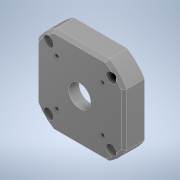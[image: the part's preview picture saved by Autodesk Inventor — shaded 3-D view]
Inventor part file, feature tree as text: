
AUTODESK INVENTOR PART (.ipt)
format: ipt  version: 2022 (Build 260153000, 153)  size: 180,224 bytes
history: mixed  units: in
note: dims shown in document units (in); Inventor stores cm internally (conversion verified against a paired STEP export)
features: extrude x2, sketch x2, chamfer x1, imported_body x1
ambient origin geometry x8: Origin, YZ Plane, XZ Plane, XY Plane, X Axis, Y Axis, Z Axis, Center Point
bodies: Solid1 (imported_parasolid)
feature tree (6):
  extrude  "Extrusion1"  Depth=0.3937in TaperAngle=0.0deg
  extrude  "Extrusion2"  Depth=0.3937in TaperAngle=0.0deg
  sketch  "Sketch1"  dims[d0=0.1102in d1=0.3937in d2=0.0in]
  sketch  "Sketch2"  dims[d3=0.5906in d4=0.3937in d5=0.0in]
  chamfer  "Chamfer2"  [1 undecoded]
  imported_body  NMx_Import_Brep_tag  [imported B-rep: ~32 faces, bbox_mm=[53.213203, 60.0, 14.0]]
note: 1 required parameter value undecoded (feature->parameter linkage not recoverable at this tier; creation-order binding heuristic only, values carry confidence <= 0.55)
